FCSTD DOCUMENT  (FreeCAD 0.19R24276 (Git))
Label: Master_sketch_v1
License: All rights reserved
LicenseURL: http://en.wikipedia.org/wiki/All_rights_reserved
objects: Sketcher::SketchObject×1, PartDesign::Body×1
note: 2 computed .brp shape members not serialized (recipe doc carries the construction recipe); baked Part::Feature solids carry a one-line shape summary decoded from their .brp

FEATURE [Sketcher::SketchObject] Sketch
  FullyConstrained = false
  MapMode = 5
  Support = -> [XY_Plane]
  sketch-geometry (15):
    g0: Circle CenterX=0 CenterY=0 CenterZ=0 NormalX=0 NormalY=0 NormalZ=1 AngleXU=0 Radius=14
    g1: Circle CenterX=62.5 CenterY=0 CenterZ=0 NormalX=0 NormalY=0 NormalZ=1 AngleXU=0 Radius=27
    g2: LineSegment StartX=-2.91197 StartY=13.6938 StartZ=0 EndX=56.884 EndY=26.4095 EndZ=0
    g3: LineSegment StartX=-2.912 StartY=-13.6938 StartZ=0 EndX=56.884 EndY=-26.4095 EndZ=0
    g4: LineSegment StartX=62.5 StartY=0 StartZ=0 EndX=56.884 EndY=26.4095 EndZ=0
    g5: LineSegment StartX=-2.91197 StartY=13.6938 StartZ=0 EndX=0 EndY=0 EndZ=0
    g6: LineSegment StartX=0 StartY=0 StartZ=0 EndX=-2.912 EndY=-13.6938 EndZ=0
    g7: LineSegment StartX=35 StartY=0 StartZ=0 EndX=62.5 EndY=0 EndZ=0
    g8: LineSegment StartX=0 StartY=0 StartZ=0 EndX=25 EndY=0 EndZ=0
    g9: LineSegment StartX=25 StartY=0 StartZ=0 EndX=25 EndY=45.442 EndZ=0
    g10: LineSegment StartX=35 StartY=0 StartZ=0 EndX=35 EndY=43.6264 EndZ=0
    g11: LineSegment StartX=33 StartY=0 StartZ=0 EndX=33 EndY=30.7772 EndZ=0
    g12: LineSegment StartX=33 StartY=0 StartZ=0 EndX=33 EndY=40.6934 EndZ=0
    g13: LineSegment StartX=62.5 StartY=0 StartZ=0 EndX=62.5 EndY=27 EndZ=0
    g14: LineSegment StartX=0 StartY=0 StartZ=0 EndX=0.0188532 EndY=14.3171 EndZ=0
  constraints (40):
    c: Coincident(g0,g-1)
    c: Diameter(g0) = 28
    c: PointOnObject(g1,g-1)
    c: Diameter(g1) = 54
    c: PointOnObject(g2,g0)
    c: PointOnObject(g2,g1)
    c: Tangent(g2,g0)
    c: PointOnObject(g3,g0)
    c: PointOnObject(g3,g1)
    c: Tangent(g3,g1)
    c: Coincident(g4,g1)
    c: Coincident(g4,g2)
    c: Coincident(g5,g2)
    c: Coincident(g5,g0)
    c: Coincident(g6,g0)
    c: Coincident(g6,g3)
    c: Perpendicular(g3,g6)
    c: Perpendicular(g2,g4)
    c: PointOnObject(g7,g-1)
    c: Coincident(g8,g0)
    c: PointOnObject(g8,g-1)
    c: DistanceX(g8,g8) = 25
    c: Coincident(g9,g8)
    c: Vertical(g9)
    c: Coincident(g7,g1)
    c: DistanceX(g7,g1) = 27.5
    c: Coincident(g10,g7)
    c: Vertical(g10)
    c: PointOnObject(g11,g-1)
    c: Vertical(g11)
    c: DistanceX(g11,g7) = 2
    c: PointOnObject(g12,g-1)
    c: Vertical(g12)
    c: DistanceX(g8,g12) = 8
    c: DistanceX(g12,g11) = 0
    c: Coincident(g13,g1)
    c: Vertical(g13)
    c: PointOnObject(g13,g1)
    c: Coincident(g14,g0)
    c: PointOnObject(g14,g2)
FEATURE [PartDesign::Body] Body
  Group = -> [Sketch]
  Origin = -> Origin
